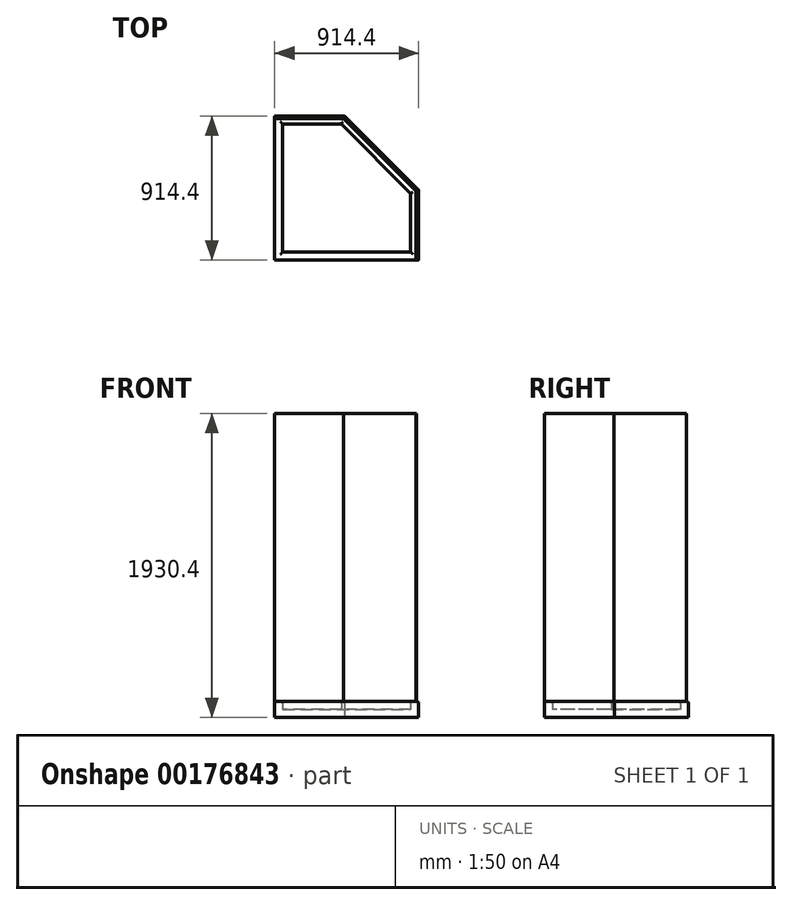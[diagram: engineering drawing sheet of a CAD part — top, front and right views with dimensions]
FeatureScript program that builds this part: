
annotation { "Feature Type Name" : "Feature", "Feature Type Description" : "" }
export const myFeature = defineFeature(function(context is Context, id is Id, definition is map)
    precondition{}
    {
        {
            var Q0;
            Q0=qCreatedBy(makeId("Top.planeOp"),FACE);
            var sketch = newSketch(context, id + "F0", { "sketchPlane" : qUnion([Q0])});
            skLineSegment(sketch, "E0", {"start": v(0, 0) * mm, "end": v(914.4, 0) * mm});
            skLineSegment(sketch, "E1", {"start": v(914.4, 444.5) * mm, "end": v(444.5, 914.4) * mm});
            skLineSegment(sketch, "E2", {"start": v(444.5, 914.4) * mm, "end": v(0, 914.4) * mm});
            skLineSegment(sketch, "E3", {"start": v(0, 914.4) * mm, "end": v(0, 0) * mm});
            skLineSegment(sketch, "E4", {"start": v(914.4, 444.5) * mm, "end": v(914.4, 0) * mm});
            skSolve(sketch);
        }
        {
            var Q0;
            Q0=qSketchRegion(id+"F0",true);
            extrude(context, id + "F1", {"entities" : qUnion([Q0]), "depth" : 101.6 * mm});
        }
        {
            var Q0;
            Q0=makeQuery(id+"F1.opExtrude","CAP_FACE",FACE,{"disambiguationData":[OSD([sQuery(id+"F0.wireOp",EDGE,"E0"),sQuery(id+"F0.wireOp",EDGE,"E1"),sQuery(id+"F0.wireOp",EDGE,"E2"),sQuery(id+"F0.wireOp",EDGE,"E3"),sQuery(id+"F0.wireOp",EDGE,"E4")])],"isStart":false});
            shell(context, id + "F2", {"entities" : qUnion([Q0]), "thickness" : 50.8 * mm});
        }
        {
            var Q0;
            Q0=makeQuery(id+"F1.opExtrude","CAP_EDGE",EDGE,{"disambiguationData":[OSD([sQuery(id+"F0.wireOp",EDGE,"E4")])],"isStart":false});
            var Q1;
            Q1=makeQuery(id+"F1.opExtrude","CAP_EDGE",EDGE,{"disambiguationData":[OSD([sQuery(id+"F0.wireOp",EDGE,"E1")])],"isStart":false});
            var Q2;
            Q2=makeQuery(id+"F1.opExtrude","CAP_EDGE",EDGE,{"disambiguationData":[OSD([sQuery(id+"F0.wireOp",EDGE,"E2")])],"isStart":false});
            var Q3;
            {var subQ0=sQuery(id+"F0.wireOp",EDGE,"E1");Q3=makeQuery(id+"F2.opShell","OFFSET_EDGE",EDGE,{"disambiguationData":[OSD([subQ0]),TDD([makeQuery(id+"F1.opExtrude","CAP_EDGE",EDGE,{"disambiguationData":[OSD([subQ0])],"isStart":false})])]});}
            var Q4;
            {var subQ0=sQuery(id+"F0.wireOp",EDGE,"E4");Q4=makeQuery(id+"F2.opShell","OFFSET_EDGE",EDGE,{"disambiguationData":[OSD([subQ0]),TDD([makeQuery(id+"F1.opExtrude","CAP_EDGE",EDGE,{"disambiguationData":[OSD([subQ0])],"isStart":false})])]});}
            var Q5;
            {var subQ0=sQuery(id+"F0.wireOp",EDGE,"E0");Q5=makeQuery(id+"F2.opShell","OFFSET_EDGE",EDGE,{"disambiguationData":[OSD([subQ0]),TDD([makeQuery(id+"F1.opExtrude","CAP_EDGE",EDGE,{"disambiguationData":[OSD([subQ0])],"isStart":false})])]});}
            var Q6;
            {var subQ0=sQuery(id+"F0.wireOp",EDGE,"E3");Q6=makeQuery(id+"F2.opShell","OFFSET_EDGE",EDGE,{"disambiguationData":[OSD([subQ0]),TDD([makeQuery(id+"F1.opExtrude","CAP_EDGE",EDGE,{"disambiguationData":[OSD([subQ0])],"isStart":false})])]});}
            var Q7;
            {var subQ0=sQuery(id+"F0.wireOp",EDGE,"E2");Q7=makeQuery(id+"F2.opShell","OFFSET_EDGE",EDGE,{"disambiguationData":[OSD([subQ0]),TDD([makeQuery(id+"F1.opExtrude","CAP_EDGE",EDGE,{"disambiguationData":[OSD([subQ0])],"isStart":false})])]});}
            fillet(context, id + "F3", {"entities" : qUnion([Q0, Q1, Q2, Q3, Q4, Q5, Q6, Q7]), "radius" : 12.7 * mm, "tangentPropagation" : true, "allowEdgeOverflow" : false});
        }
        {
            var Q0;
            Q0=makeQuery(id+"F1.opExtrude","CAP_FACE",FACE,{"disambiguationData":[OSD([sQuery(id+"F0.wireOp",EDGE,"E0"),sQuery(id+"F0.wireOp",EDGE,"E1"),sQuery(id+"F0.wireOp",EDGE,"E2"),sQuery(id+"F0.wireOp",EDGE,"E3"),sQuery(id+"F0.wireOp",EDGE,"E4")])],"isStart":false});
            var sketch = newSketch(context, id + "F4", { "sketchPlane" : qUnion([Q0])});
            skLineSegment(sketch, "E5", {"start": v(901.7, 0) * mm, "end": v(901.7, 439.24) * mm});
            skLineSegment(sketch, "E6", {"start": v(901.7, 439.24) * mm, "end": v(439.24, 901.7) * mm});
            skLineSegment(sketch, "E7", {"start": v(439.24, 901.7) * mm, "end": v(0, 901.7) * mm});
            skLineSegment(sketch, "E8.0", {"start": v(437.92, 898.53) * mm, "end": v(0, 898.53) * mm});
            skLineSegment(sketch, "E8.1", {"start": v(898.53, 437.92) * mm, "end": v(437.92, 898.53) * mm});
            skLineSegment(sketch, "E8.2", {"start": v(898.53, 0) * mm, "end": v(898.53, 437.92) * mm});
            skLineSegment(sketch, "E9", {"start": v(0, 901.7) * mm, "end": v(0, 898.53) * mm});
            skLineSegment(sketch, "E10", {"start": v(898.53, 0) * mm, "end": v(901.7, 0) * mm});
            skSolve(sketch);
        }
        {
            var Q0;
            Q0=qSketchRegion(id+"F4",true);
            extrude(context, id + "F5", {"entities" : qUnion([Q0]), "depth" : 1828.8 * mm});
        }
    });
